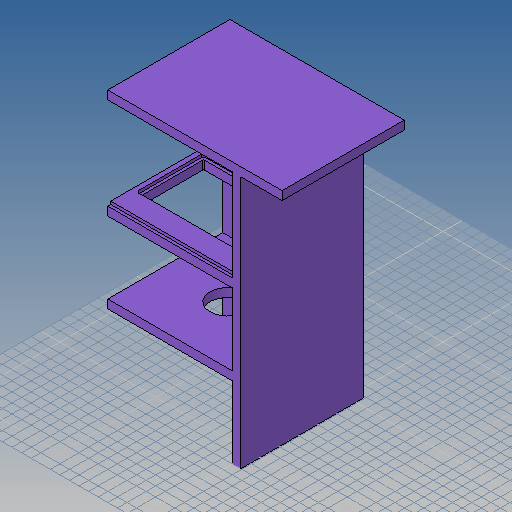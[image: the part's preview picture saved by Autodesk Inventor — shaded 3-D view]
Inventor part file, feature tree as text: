
AUTODESK INVENTOR PART (.ipt)
format: ipt  version: 2019 (Build 230136000, 136)  size: 218,112 bytes
history: native  units: mm
features: extrude x7, other x6, sketch x5, reference x1
ambient origin geometry x8: Origin, YZ Plane, XZ Plane, XY Plane, X Axis, Y Axis, Z Axis, Center Point
bodies: Volumenkörper1 (feature_tree)
feature tree (19):
  other  "<userpath>\OneDrive\Dokumente\Inventor\Absauganlage\Absauganlage_Params.xlsx"
  sketch  "Skizze1"  dims[d0=18.0mm d1=15.0mm]
  extrude  "Extrusion1"  Depth=15.0mm
  extrude  "Extrusion7"  Depth=255.0mm
  extrude  "Extrusion2"  Depth=260.0mm TaperAngle=0.0deg
  extrude  "Extrusion4"  Depth=364.0mm
  extrude  "Extrusion8"  Depth=50.0mm
  sketch  "Skizze9"  dims[d11=0.0mm d16=50.0mm d17=364.0mm d18=0.0mm d23=150.0mm d26=104.0mm d27=0.0mm d28=18.0mm d29=0.0mm d49=18.0mm d50=150.0mm d51=192.0mm d52=255.0mm d53=140.0mm d54=240.0mm d55=5.0mm d56=232.0mm d57=132.0mm d58=2.0mm d59=128.0mm d60=228.0mm d61=2.0mm d63=120.0mm d64=0.0mm d65=6.0mm d66=0.0mm d67=6.0mm]
  extrude  "Extrusion11"  Depth=364.0mm
  extrude  "Extrusion12"  TaperAngle=0.0deg  [1 undecoded]
  sketch  "Skizze2"  dims[d2=18.0mm d5=255.0mm]
  sketch  "Skizze4"  dims[d6=360.0mm d7=260.0mm d8=0.0mm]
  reference  "Referenz2"
  sketch  "Skizze6"  dims[d9=73.0mm d10=364.0mm]
  other  "<userpath>\OneDrive\Dokumente\Inventor\Absauganlage\Absauganlage.iam"
  other  "Absauganlage.iam"
  other  "Zyklon:1"
  other  "HT-50_Bogen_45grd-3-64:1"
  other  "Schnittkanten projizieren1"
note: 1 required parameter value undecoded (feature->parameter linkage not recoverable at this tier; creation-order binding heuristic only, values carry confidence <= 0.55)
